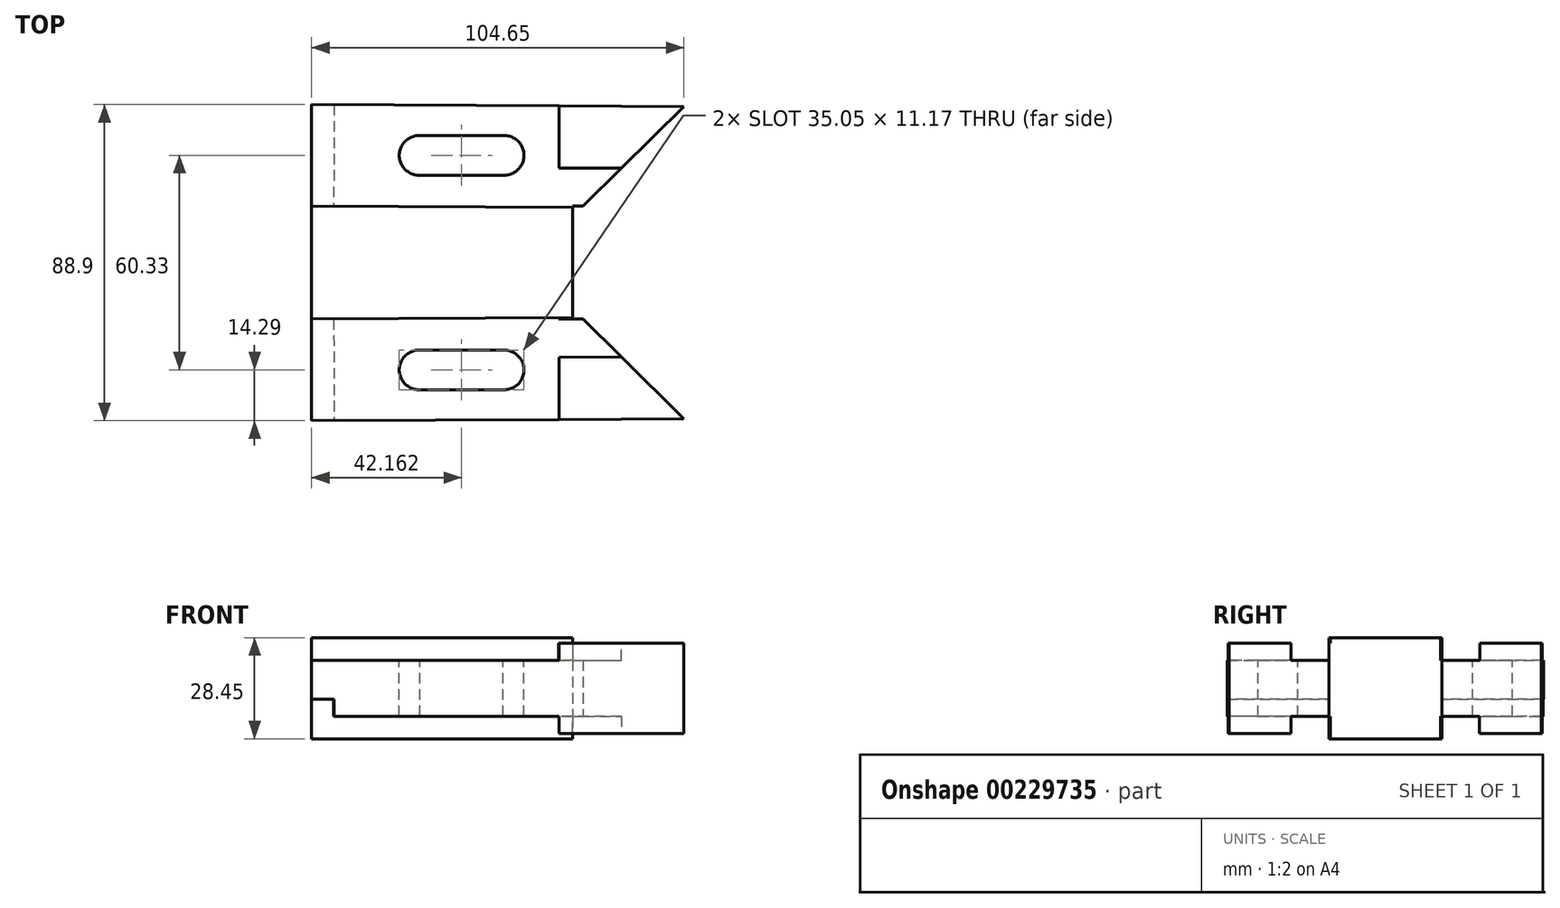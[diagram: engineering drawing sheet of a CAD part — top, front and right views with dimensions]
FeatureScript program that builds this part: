
annotation { "Feature Type Name" : "Feature", "Feature Type Description" : "" }
export const myFeature = defineFeature(function(context is Context, id is Id, definition is map)
    precondition{}
    {
        {
            var Q0;
            Q0=qCreatedBy(makeId("Top.planeOp"),FACE);
            var sketch = newSketch(context, id + "F0", { "sketchPlane" : qUnion([Q0])});
            skLineSegment(sketch, "E0", {"start": v(-30.47, 28.57) * mm, "end": v(74.18, 28.03) * mm});
            skLineSegment(sketch, "E1", {"start": v(-30.47, 28.57) * mm, "end": v(-30.47, 0) * mm});
            skLineSegment(sketch, "E2", {"start": v(-30.47, 0) * mm, "end": v(-30.47, -15.87) * mm});
            skPoint(sketch, "E3.end.orphan", {"position": v(45.85, 0) * mm});
            skLineSegment(sketch, "E4", {"start": v(74.18, 28.03) * mm, "end": v(45.85, 0) * mm});
            skLineSegment(sketch, "E5", {"start": v(-30.47, 0) * mm, "end": v(42.93, 0) * mm});
            skLineSegment(sketch, "E6", {"start": v(42.93, 0) * mm, "end": v(42.93, -15.87) * mm});
            skLineSegment(sketch, "E7", {"start": v(45.85, 0) * mm, "end": v(42.93, 0) * mm});
            skLineSegment(sketch, "E8", {"start": v(-30.47, -15.87) * mm, "end": v(42.93, -15.87) * mm});
            skPoint(sketch, "E9.start.orphan", {"position": v(-30.47, -31.75) * mm});
            skPoint(sketch, "E10.orphan", {"position": v(42.93, -31.75) * mm});
            skLineSegment(sketch, "E11.MirrorCS", {"start": v(-30.47, -31.75) * mm, "end": v(-30.47, -15.87) * mm});
            skLineSegment(sketch, "E12.MirrorCS", {"start": v(-30.47, -60.32) * mm, "end": v(-30.47, -31.75) * mm});
            skLineSegment(sketch, "E13.MirrorCS", {"start": v(-30.47, -60.32) * mm, "end": v(74.18, -59.78) * mm});
            skLineSegment(sketch, "E14.MirrorCS", {"start": v(74.18, -59.78) * mm, "end": v(45.85, -31.75) * mm});
            skLineSegment(sketch, "E15.MirrorCS", {"start": v(42.93, -31.75) * mm, "end": v(42.93, -15.87) * mm});
            skLineSegment(sketch, "E16.MirrorCS", {"start": v(45.85, -31.75) * mm, "end": v(42.93, -31.75) * mm});
            skSolve(sketch);
        }
        {
            var Q0;
            Q0 = qSketchRegion(id + "F0", true);
            extrude(context, id + "F1", {"entities" : qUnion([Q0]), "depth" : 28.45 * mm});
        }
        {
            var Q0;
            Q0=makeQuery(id+"F1.opExtrude","SWEPT_FACE",FACE,{"disambiguationData":[OSD([sQuery(id+"F0.wireOp",EDGE,"E13.MirrorCS")])]});
            var sketch = newSketch(context, id + "F2", { "sketchPlane" : qUnion([Q0])});
            skLineSegment(sketch, "E17", {"start": v(-30.78, 0) * mm, "end": v(-30.78, 1.52) * mm});
            skLineSegment(sketch, "E18", {"start": v(-30.78, 1.52) * mm, "end": v(-30.78, 26.92) * mm});
            skLineSegment(sketch, "E19", {"start": v(-30.78, 26.92) * mm, "end": v(-30.78, 28.45) * mm});
            skPoint(sketch, "E20.startSnap0", {"position": v(21.54, 28.45) * mm});
            skLineSegment(sketch, "E21.MirrorCS", {"start": v(73.87, 26.92) * mm, "end": v(73.87, 28.45) * mm});
            skLineSegment(sketch, "E22.MirrorCS", {"start": v(73.87, 0) * mm, "end": v(73.87, 1.52) * mm});
            skLineSegment(sketch, "E23", {"start": v(-30.78, 28.45) * mm, "end": v(38.81, 28.45) * mm});
            skLineSegment(sketch, "E24", {"start": v(38.81, 28.45) * mm, "end": v(38.81, 26.92) * mm});
            skLineSegment(sketch, "E25", {"start": v(38.81, 26.92) * mm, "end": v(73.87, 26.92) * mm});
            skLineSegment(sketch, "E26", {"start": v(38.81, 26.92) * mm, "end": v(38.81, 0) * mm});
            skLineSegment(sketch, "E27", {"start": v(73.87, 1.52) * mm, "end": v(38.81, 1.52) * mm});
            skLineSegment(sketch, "E28", {"start": v(38.81, 28.45) * mm, "end": v(73.87, 28.45) * mm});
            skSolve(sketch);
        }
        {
            var Q0;
            Q0 = qSketchRegion(id + "F2", true);
            var Q1;
            {var subQ0=sQuery(id+"F2.wireOp",EDGE,"E22.MirrorCS");Q1=makeQuery(id+"F2.imprint","IMPRINT",FACE,{"disambiguationData":[TD([[makeQuery(id+"F2.imprint","IMPRINT",EDGE,{"derivedFrom":subQ0}),-1.0]])]});}
            extrude(context, id + "F3", {"entities" : qUnion([Q0, Q1]), "operationType" : NewBodyOperationType.REMOVE, "oppositeDirection" : true, "depth" : 28.57 * mm});
        }
        {
            var Q0;
            Q0=makeQuery(id+"F1.opExtrude","SWEPT_FACE",FACE,{"disambiguationData":[OSD([sQuery(id+"F0.wireOp",EDGE,"E13.MirrorCS")])]});
            var sketch = newSketch(context, id + "F4", { "sketchPlane" : qUnion([Q0])});
            skLineSegment(sketch, "E29", {"start": v(-30.78, 28.45) * mm, "end": v(-30.78, 22.1) * mm});
            skLineSegment(sketch, "E30", {"start": v(-30.78, 22.1) * mm, "end": v(-30.78, 11.18) * mm});
            skLineSegment(sketch, "E31", {"start": v(-30.78, 11.18) * mm, "end": v(-24.43, 11.18) * mm});
            skLineSegment(sketch, "E32", {"start": v(-24.43, 11.18) * mm, "end": v(-24.43, 6.35) * mm});
            skLineSegment(sketch, "E33", {"start": v(-24.43, 6.35) * mm, "end": v(38.81, 6.35) * mm});
            skLineSegment(sketch, "E34", {"start": v(38.81, 6.35) * mm, "end": v(38.81, 0) * mm});
            skLineSegment(sketch, "E35", {"start": v(-30.78, 22.1) * mm, "end": v(38.81, 22.1) * mm});
            skLineSegment(sketch, "E36", {"start": v(38.81, 22.1) * mm, "end": v(38.81, 28.45) * mm});
            skLineSegment(sketch, "E37", {"start": v(38.81, 28.45) * mm, "end": v(-30.78, 28.45) * mm});
            skLineSegment(sketch, "E38", {"start": v(-30.78, 11.18) * mm, "end": v(-30.78, 0) * mm});
            skLineSegment(sketch, "E39", {"start": v(-30.78, 0) * mm, "end": v(38.81, 0) * mm});
            skSolve(sketch);
        }
        {
            var Q0;
            Q0 = qSketchRegion(id + "F4", true);
            extrude(context, id + "F5", {"entities" : qUnion([Q0]), "operationType" : NewBodyOperationType.REMOVE, "oppositeDirection" : true, "depth" : 28.57 * mm});
        }
        {
            var Q0;
            Q0=makeQuery(id+"F3.boolean.opBoolean","COPY",FACE,{"derivedFrom":makeQuery(id+"F3.opExtrude","SWEPT_FACE",FACE,{"disambiguationData":[OSD([sQuery(id+"F2.wireOp",EDGE,"E25")])]})});
            var sketch = newSketch(context, id + "F6", { "sketchPlane" : qUnion([Q0])});
            skLineSegment(sketch, "E40", {"start": v(38.98, -31.4) * mm, "end": v(39.03, -42.44) * mm});
            skLineSegment(sketch, "E41", {"start": v(56.56, -42.35) * mm, "end": v(45.85, -31.75) * mm});
            skLineSegment(sketch, "E42", {"start": v(45.85, -31.75) * mm, "end": v(38.98, -31.75) * mm});
            skLineSegment(sketch, "E43", {"start": v(38.98, -31.75) * mm, "end": v(38.98, -31.4) * mm});
            skLineSegment(sketch, "E44", {"start": v(42.93, -31.37) * mm, "end": v(42.93, -31.75) * mm});
            skLineSegment(sketch, "E45", {"start": v(39.03, -42.44) * mm, "end": v(56.56, -42.35) * mm});
            skSolve(sketch);
        }
        {
            var Q0;
            Q0 = qSketchRegion(id + "F6", true);
            var Q1;
            {var subQ2=sQuery(id+"F6.wireOp",EDGE,"E43");Q1=makeQuery(id+"F6.imprint","IMPRINT",FACE,{"disambiguationData":[TD([[makeQuery(id+"F6.imprint","IMPRINT",EDGE,{"derivedFrom":subQ2}),1.0]])]});}
            extrude(context, id + "F7", {"entities" : qUnion([Q0, Q1]), "operationType" : NewBodyOperationType.REMOVE, "oppositeDirection" : true, "depth" : 4.83 * mm});
        }
        {
            var Q0;
            Q0=makeQuery(id+"F1.opExtrude","SWEPT_FACE",FACE,{"disambiguationData":[OSD([sQuery(id+"F0.wireOp",EDGE,"E0")])]});
            var sketch = newSketch(context, id + "F8", { "sketchPlane" : qUnion([Q0])});
            skLineSegment(sketch, "E46", {"start": v(-74.03, 28.45) * mm, "end": v(-74.03, 26.92) * mm});
            skLineSegment(sketch, "E47", {"start": v(-74.03, 26.92) * mm, "end": v(-74.03, 1.52) * mm});
            skLineSegment(sketch, "E48", {"start": v(-74.03, 1.52) * mm, "end": v(-74.03, 0) * mm});
            skLineSegment(sketch, "E49", {"start": v(-74.03, 26.92) * mm, "end": v(-48.64, 26.92) * mm});
            skLineSegment(sketch, "E50", {"start": v(-48.64, 28.45) * mm, "end": v(30.62, 28.45) * mm});
            skLineSegment(sketch, "E51", {"start": v(-74.03, 28.45) * mm, "end": v(-48.64, 28.45) * mm});
            skLineSegment(sketch, "E52", {"start": v(-74.03, 0) * mm, "end": v(-49.05, 0) * mm});
            skLineSegment(sketch, "E53", {"start": v(-48.64, 26.92) * mm, "end": v(30.62, 26.92) * mm});
            skLineSegment(sketch, "E54", {"start": v(30.62, 26.92) * mm, "end": v(30.62, 28.45) * mm});
            skLineSegment(sketch, "E55", {"start": v(-74.03, 1.52) * mm, "end": v(30.62, 1.52) * mm});
            skLineSegment(sketch, "E56", {"start": v(30.62, 1.52) * mm, "end": v(30.62, 0) * mm});
            skLineSegment(sketch, "E57", {"start": v(30.62, 0) * mm, "end": v(-49.05, 0) * mm});
            skSolve(sketch);
        }
        {
            var Q0;
            Q0 = qSketchRegion(id + "F8", true);
            extrude(context, id + "F9", {"entities" : qUnion([Q0]), "operationType" : NewBodyOperationType.REMOVE, "oppositeDirection" : true, "depth" : 28.57 * mm});
        }
        {
            var Q0;
            Q0=makeQuery(id+"F9.boolean.opBoolean","COPY",FACE,{"derivedFrom":makeQuery(id+"F9.opExtrude","SWEPT_FACE",FACE,{"disambiguationData":[OSD([sQuery(id+"F8.wireOp",EDGE,"E49"),sQuery(id+"F8.wireOp",EDGE,"E53")])]})});
            var sketch = newSketch(context, id + "F10", { "sketchPlane" : qUnion([Q0])});
            skLineSegment(sketch, "E58", {"start": v(39.12, 28.22) * mm, "end": v(39.12, 10.69) * mm});
            skLineSegment(sketch, "E59", {"start": v(39.12, 10.69) * mm, "end": v(56.65, 10.69) * mm});
            skLineSegment(sketch, "E60", {"start": v(39.12, 28.22) * mm, "end": v(-30.47, 28.57) * mm});
            skLineSegment(sketch, "E61", {"start": v(-30.47, 28.57) * mm, "end": v(-30.47, 0) * mm});
            skLineSegment(sketch, "E62", {"start": v(45.85, 0) * mm, "end": v(56.65, 10.69) * mm});
            skLineSegment(sketch, "E63", {"start": v(-30.47, 0) * mm, "end": v(42.93, -0.38) * mm});
            skLineSegment(sketch, "E64", {"start": v(42.93, -0.38) * mm, "end": v(42.93, 0) * mm});
            skLineSegment(sketch, "E65", {"start": v(42.93, 0) * mm, "end": v(45.85, 0) * mm});
            skSolve(sketch);
        }
        {
            var Q0;
            Q0 = qSketchRegion(id + "F10", true);
            extrude(context, id + "F11", {"entities" : qUnion([Q0]), "operationType" : NewBodyOperationType.REMOVE, "oppositeDirection" : true, "depth" : 4.83 * mm});
        }
        {
            var Q0;
            Q0=makeQuery(id+"F9.boolean.opBoolean","COPY",FACE,{"derivedFrom":makeQuery(id+"F9.opExtrude","SWEPT_FACE",FACE,{"disambiguationData":[OSD([sQuery(id+"F8.wireOp",EDGE,"E55")])]})});
            var sketch = newSketch(context, id + "F12", { "sketchPlane" : qUnion([Q0])});
            skLineSegment(sketch, "E66", {"start": v(-30.47, -28.57) * mm, "end": v(-24.12, -28.54) * mm});
            skLineSegment(sketch, "E67", {"start": v(-24.12, -28.54) * mm, "end": v(-24.27, 0.03) * mm});
            skLineSegment(sketch, "E68", {"start": v(-24.27, 0.03) * mm, "end": v(-30.47, 0) * mm});
            skLineSegment(sketch, "E69", {"start": v(-30.47, 0) * mm, "end": v(-30.47, -28.57) * mm});
            skSolve(sketch);
        }
        {
            var Q0;
            Q0 = qSketchRegion(id + "F12", true);
            extrude(context, id + "F13", {"entities" : qUnion([Q0]), "operationType" : NewBodyOperationType.REMOVE, "oppositeDirection" : true, "depth" : 9.65 * mm});
        }
        {
            var Q0;
            Q0=makeQuery(id+"F9.boolean.opBoolean","COPY",FACE,{"derivedFrom":makeQuery(id+"F9.opExtrude","SWEPT_FACE",FACE,{"disambiguationData":[OSD([sQuery(id+"F8.wireOp",EDGE,"E55")])]})});
            var sketch = newSketch(context, id + "F14", { "sketchPlane" : qUnion([Q0])});
            skLineSegment(sketch, "E70", {"start": v(-24.27, 0.03) * mm, "end": v(38.98, 0.36) * mm});
            skLineSegment(sketch, "E71", {"start": v(38.98, 0.36) * mm, "end": v(39.12, -28.22) * mm});
            skLineSegment(sketch, "E72", {"start": v(39.12, -28.22) * mm, "end": v(-24.12, -28.54) * mm});
            skLineSegment(sketch, "E73", {"start": v(-24.12, -28.54) * mm, "end": v(-24.27, 0.03) * mm});
            skSolve(sketch);
        }
        {
            var Q0;
            Q0 = qSketchRegion(id + "F14", true);
            extrude(context, id + "F15", {"entities" : qUnion([Q0]), "operationType" : NewBodyOperationType.REMOVE, "oppositeDirection" : true, "depth" : 4.83 * mm});
        }
        {
            var Q0;
            Q0=makeQuery(id+"F15.boolean.opBoolean","COPY",FACE,{"derivedFrom":makeQuery(id+"F15.opExtrude","SWEPT_FACE",FACE,{"disambiguationData":[OSD([sQuery(id+"F14.wireOp",EDGE,"E71")])]})});
            var sketch = newSketch(context, id + "F16", { "sketchPlane" : qUnion([Q0])});
            skLineSegment(sketch, "E74", {"start": v(-0.21, 6.35) * mm, "end": v(-10.9, 6.35) * mm});
            skLineSegment(sketch, "E75", {"start": v(-10.9, 6.35) * mm, "end": v(-10.9, 1.52) * mm});
            skLineSegment(sketch, "E76", {"start": v(-10.9, 1.52) * mm, "end": v(-0.21, 1.52) * mm});
            skLineSegment(sketch, "E77", {"start": v(-10.9, 6.35) * mm, "end": v(-28.42, 6.35) * mm});
            skLineSegment(sketch, "E78", {"start": v(0.16, 1.52) * mm, "end": v(0.16, 6.35) * mm});
            skLineSegment(sketch, "E79", {"start": v(0.16, 6.35) * mm, "end": v(-0.21, 6.35) * mm});
            skLineSegment(sketch, "E80", {"start": v(0.16, 1.52) * mm, "end": v(-0.21, 1.52) * mm});
            skSolve(sketch);
        }
        {
            var Q0;
            Q0 = qSketchRegion(id + "F16", true);
            extrude(context, id + "F17", {"entities" : qUnion([Q0]), "operationType" : NewBodyOperationType.REMOVE, "oppositeDirection" : true, "depth" : 25.4 * mm});
        }
        {
            var Q0;
            Q0=makeQuery(id+"F5.boolean.opBoolean","COPY",FACE,{"derivedFrom":makeQuery(id+"F5.opExtrude","SWEPT_FACE",FACE,{"disambiguationData":[OSD([sQuery(id+"F4.wireOp",EDGE,"E34")])]})});
            var sketch = newSketch(context, id + "F18", { "sketchPlane" : qUnion([Q0])});
            skLineSegment(sketch, "E81", {"start": v(31.6, 6.35) * mm, "end": v(42.64, 6.35) * mm});
            skLineSegment(sketch, "E82", {"start": v(42.64, 6.35) * mm, "end": v(42.64, 1.52) * mm});
            skLineSegment(sketch, "E83", {"start": v(42.64, 1.52) * mm, "end": v(31.6, 1.52) * mm});
            skLineSegment(sketch, "E84", {"start": v(31.6, 1.52) * mm, "end": v(31.6, 6.35) * mm});
            skLineSegment(sketch, "E85", {"start": v(42.64, 6.35) * mm, "end": v(60.17, 6.35) * mm});
            skSolve(sketch);
        }
        {
            var Q0;
            Q0 = qSketchRegion(id + "F18", true);
            extrude(context, id + "F19", {"entities" : qUnion([Q0]), "operationType" : NewBodyOperationType.REMOVE, "oppositeDirection" : true, "depth" : 25.4 * mm});
        }
        {
            var Q0;
            Q0=makeQuery(id+"F7.boolean.opBoolean","MERGE",FACE,{"derivedFrom":[makeQuery(id+"F5.boolean.opBoolean","COPY",FACE,{"derivedFrom":makeQuery(id+"F5.opExtrude","SWEPT_FACE",FACE,{"disambiguationData":[OSD([sQuery(id+"F4.wireOp",EDGE,"E35")])]})}),makeQuery(id+"F7.opExtrude","CAP_FACE",FACE,{"disambiguationData":[OSD([sQuery(id+"F2.wireOp",EDGE,"E25"),sQuery(id+"F6.wireOp",EDGE,"E40"),sQuery(id+"F6.wireOp",EDGE,"E41"),sQuery(id+"F6.wireOp",EDGE,"E42"),sQuery(id+"F6.wireOp",EDGE,"E43"),sQuery(id+"F6.wireOp",EDGE,"E44"),sQuery(id+"F6.wireOp",EDGE,"E45")])],"isStart":false})]});
            var sketch = newSketch(context, id + "F20", { "sketchPlane" : qUnion([Q0])});
            skLineSegment(sketch, "E86", {"start": v(-30.47, -31.75) * mm, "end": v(-30.47, -60.32) * mm});
            skArc(sketch, "E87", {"start": v(23.63, -51.63) * mm, "mid": v(29.22, -45.92) * mm, "end": v(23.38, -40.45) * mm});
            skArc(sketch, "E88", {"start": v(0, -40.45) * mm, "mid": v(-5.83, -46.04) * mm, "end": v(0, -51.62) * mm});
            skLineSegment(sketch, "E89", {"start": v(-30.47, -15.87) * mm, "end": v(12.3, -15.87) * mm});
            skArc(sketch, "E90.MirrorC", {"start": v(0, 8.7) * mm, "mid": v(-5.83, 14.29) * mm, "end": v(0, 19.87) * mm});
            skArc(sketch, "E91.MirrorC", {"start": v(23.63, 19.88) * mm, "mid": v(29.22, 14.17) * mm, "end": v(23.38, 8.7) * mm});
            skPoint(sketch, "E92.start.orphan", {"position": v(-30.47, 14.29) * mm});
            skPoint(sketch, "E93.start.orphan", {"position": v(-30.47, -46.04) * mm});
            skPoint(sketch, "E94.orphan", {"position": v(-30.47, 28.58) * mm});
            skPoint(sketch, "E95.orphan", {"position": v(-30.47, 0) * mm});
            skPoint(sketch, "E96.trimOffspring.end.orphan", {"position": v(29.22, 14.29) * mm});
            skPoint(sketch, "E97.MirrorCS.start.orphan", {"position": v(-5.83, 14.29) * mm});
            skPoint(sketch, "E98.start.orphan", {"position": v(-5.83, -46.04) * mm});
            skPoint(sketch, "E99.trimOffspring.end.orphan", {"position": v(29.22, -46.04) * mm});
            skLineSegment(sketch, "E100", {"start": v(0, -51.62) * mm, "end": v(23.63, -51.63) * mm});
            skLineSegment(sketch, "E101", {"start": v(0, -40.45) * mm, "end": v(23.38, -40.45) * mm});
            skLineSegment(sketch, "E102.MirrorCS", {"start": v(0, 8.7) * mm, "end": v(23.38, 8.7) * mm});
            skLineSegment(sketch, "E103.MirrorCS", {"start": v(0, 19.87) * mm, "end": v(23.63, 19.88) * mm});
            skSolve(sketch);
        }
        {
            var Q0;
            Q0 = qSketchRegion(id + "F20", true);
            extrude(context, id + "F21", {"entities" : qUnion([Q0]), "operationType" : NewBodyOperationType.REMOVE, "oppositeDirection" : true, "depth" : 25.4 * mm});
        }
    });
